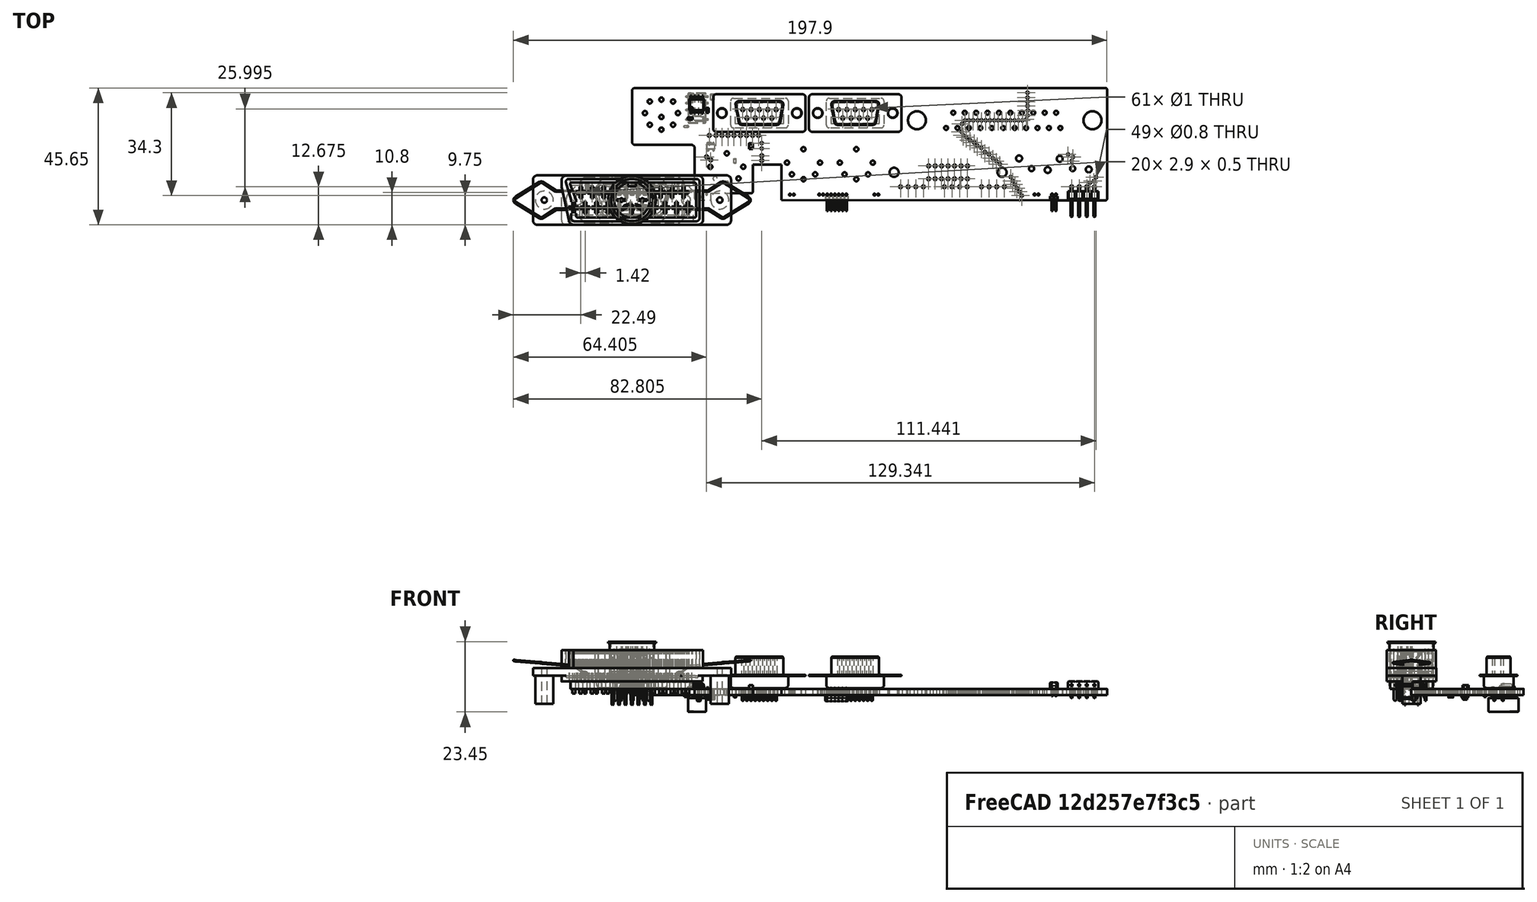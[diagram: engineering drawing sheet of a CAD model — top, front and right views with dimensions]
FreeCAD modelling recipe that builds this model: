
FCSTD DOCUMENT  (FreeCAD 0.20R29177 (Git))
Label: Ultra-IO-shield-2
License: All rights reserved
LicenseURL: http://en.wikipedia.org/wiki/All_rights_reserved
objects: Part::Feature×85, App::Link×60, App::Part×16, PartDesign::CoordinateSystem×1, Sketcher::SketchObject×1
note: 87 computed .brp shape members not serialized (recipe doc carries the construction recipe); baked Part::Feature solids carry a one-line shape summary decoded from their .brp

FEATURE [PartDesign::CoordinateSystem] Local_CS_8e65
  AttacherType = Attacher::AttachEngine3D
FEATURE [Part::Feature] Pcb_8e65
  Placement = pos=(-90.355,111.3,0) rot=(0,0,1;0rad)
  shape: bbox 158.3 x 37.53 x 2 mm, 212 faces (baked)
FEATURE [Sketcher::SketchObject] PCB_Sketch_8e65
  FullyConstrained = false
  sketch-geometry (81):
    g0: LineSegment StartX=40.245 StartY=11.8 StartZ=0 EndX=49.845 EndY=11.8 EndZ=0
    g1: LineSegment StartX=21.345 StartY=8e-16 StartZ=0 EndX=26.245 EndY=0 EndZ=0
    g2: LineSegment StartX=1 StartY=37.4 StartZ=0 EndX=157.845 EndY=37.4 EndZ=0
    g3: LineSegment StartX=49.845 StartY=-0.018571 StartZ=0 EndX=157.845 EndY=-0.13 EndZ=0
    g4: LineSegment StartX=40.245 StartY=11.8 StartZ=0 EndX=40.245 EndY=2.7375 EndZ=0
    g5: LineSegment StartX=20.845 StartY=0.5 StartZ=0 EndX=20.845 EndY=17.4 EndZ=0
    g6: LineSegment StartX=1 StartY=18.4 StartZ=0 EndX=19.845 EndY=18.4 EndZ=0
    g7: LineSegment StartX=1.7e-15 StartY=36.4 StartZ=0 EndX=-8e-16 EndY=19.4 EndZ=0
    g8: LineSegment StartX=26.245 StartY=2.2375 StartZ=0 EndX=39.745 EndY=2.2375 EndZ=0
    g9: LineSegment StartX=26.245 StartY=2.2375 StartZ=0 EndX=26.245 EndY=0 EndZ=0
    g10: LineSegment StartX=158.345 StartY=36.9 StartZ=0 EndX=158.345 EndY=0.37 EndZ=0
    g11: LineSegment StartX=49.845 StartY=11.8 StartZ=0 EndX=49.845 EndY=-0.018571 EndZ=0
    g12: ArcOfCircle CenterX=39.745 CenterY=2.7375 CenterZ=0 NormalX=0 NormalY=0 NormalZ=-1 AngleXU=-3.14159 Radius=0.500001 StartAngle=0 EndAngle=1.57079
    g13: ArcOfCircle CenterX=0.999999 CenterY=36.4 CenterZ=0 NormalX=0 NormalY=0 NormalZ=-1 AngleXU=-7.47076e-07 Radius=0.999999 StartAngle=0 EndAngle=1.5708
    g14: ArcOfCircle CenterX=157.845 CenterY=36.9 CenterZ=0 NormalX=0 NormalY=0 NormalZ=-1 AngleXU=1.5708 Radius=0.500001 StartAngle=0 EndAngle=1.57079
    g15: ArcOfCircle CenterX=21.345 CenterY=0.500001 CenterZ=0 NormalX=0 NormalY=0 NormalZ=-1 AngleXU=-1.57079 Radius=0.500001 StartAngle=0 EndAngle=1.57079
    g16: ArcOfCircle CenterX=0.999999 CenterY=19.4 CenterZ=0 NormalX=0 NormalY=0 NormalZ=-1 AngleXU=-1.5708 Radius=0.999999 StartAngle=0 EndAngle=1.5708
    g17: ArcOfCircle CenterX=19.845 CenterY=17.4 CenterZ=0 NormalX=0 NormalY=0 NormalZ=-1 AngleXU=1.5708 Radius=0.999999 StartAngle=0 EndAngle=1.5708
    g18: ArcOfCircle CenterX=157.845 CenterY=0.370001 CenterZ=0 NormalX=0 NormalY=0 NormalZ=-1 AngleXU=-3.14159 Radius=0.500001 StartAngle=0 EndAngle=1.57079
    g19: Circle CenterX=128.845 CenterY=26.6 CenterZ=0 NormalX=0 NormalY=0 NormalZ=1 AngleXU=0 Radius=0.4
    g20: Circle CenterX=33.9825 CenterY=21.5625 CenterZ=0 NormalX=0 NormalY=0 NormalZ=1 AngleXU=0 Radius=0.5
    g21: Circle CenterX=27.9825 CenterY=21.5625 CenterZ=0 NormalX=0 NormalY=0 NormalZ=1 AngleXU=0 Radius=0.5
    g22: Circle CenterX=131.445 CenterY=26.9 CenterZ=0 NormalX=0 NormalY=0 NormalZ=1 AngleXU=0 Radius=0.4
    g23: Circle CenterX=131.845 CenterY=35.8 CenterZ=0 NormalX=0 NormalY=0 NormalZ=1 AngleXU=0 Radius=0.4
    g24: Circle CenterX=152.686 CenterY=5.82926 CenterZ=0 NormalX=0 NormalY=0 NormalZ=1 AngleXU=0 Radius=0.4
    g25: Circle CenterX=25.7825 CenterY=21.5625 CenterZ=0 NormalX=0 NormalY=0 NormalZ=1 AngleXU=0 Radius=0.5
    g26: Circle CenterX=122.645 CenterY=12 CenterZ=0 NormalX=0 NormalY=0 NormalZ=1 AngleXU=0 Radius=0.4
    g27: Circle CenterX=154.686 CenterY=7.62926 CenterZ=0 NormalX=0 NormalY=0 NormalZ=1 AngleXU=0 Radius=0.4
    g28: Circle CenterX=112.345 CenterY=26.6 CenterZ=0 NormalX=0 NormalY=0 NormalZ=1 AngleXU=0 Radius=0.4
    g29: Circle CenterX=43.245 CenterY=17.2 CenterZ=0 NormalX=0 NormalY=0 NormalZ=1 AngleXU=0 Radius=0.4
    g30: Circle CenterX=42.1825 CenterY=21.5625 CenterZ=0 NormalX=0 NormalY=0 NormalZ=1 AngleXU=0 Radius=0.5
    g31: Circle CenterX=110.045 CenterY=25.4 CenterZ=0 NormalX=0 NormalY=0 NormalZ=1 AngleXU=0 Radius=0.4
    g32: Circle CenterX=129.145 CenterY=2.8 CenterZ=0 NormalX=0 NormalY=0 NormalZ=1 AngleXU=0 Radius=0.4
    g33: Circle CenterX=43.245 CenterY=14.8 CenterZ=0 NormalX=0 NormalY=0 NormalZ=1 AngleXU=0 Radius=0.5
    g34: Circle CenterX=43.245 CenterY=13.2 CenterZ=0 NormalX=0 NormalY=0 NormalZ=1 AngleXU=0 Radius=0.5
    g35: Circle CenterX=109.845 CenterY=22.8 CenterZ=0 NormalX=0 NormalY=0 NormalZ=1 AngleXU=0 Radius=0.4
    g36: Circle CenterX=115.045 CenterY=18.2 CenterZ=0 NormalX=0 NormalY=0 NormalZ=1 AngleXU=0 Radius=0.4
    g37: Circle CenterX=43.245 CenterY=19 CenterZ=0 NormalX=0 NormalY=0 NormalZ=1 AngleXU=0 Radius=0.4
    g38: Circle CenterX=113.745 CenterY=26.6 CenterZ=0 NormalX=0 NormalY=0 NormalZ=1 AngleXU=0 Radius=0.4
    g39: Circle CenterX=145.386 CenterY=15.2293 CenterZ=0 NormalX=0 NormalY=0 NormalZ=1 AngleXU=0 Radius=0.4
    g40: Circle CenterX=117.645 CenterY=16 CenterZ=0 NormalX=0 NormalY=0 NormalZ=1 AngleXU=0 Radius=0.4
    g41: Circle CenterX=110.445 CenterY=21.6 CenterZ=0 NormalX=0 NormalY=0 NormalZ=1 AngleXU=0 Radius=0.4
    g42: Circle CenterX=40.1825 CenterY=21.5625 CenterZ=0 NormalX=0 NormalY=0 NormalZ=1 AngleXU=0 Radius=0.5
    g43: Circle CenterX=120.245 CenterY=14 CenterZ=0 NormalX=0 NormalY=0 NormalZ=1 AngleXU=0 Radius=0.4
    g44: Circle CenterX=122.045 CenterY=26.6 CenterZ=0 NormalX=0 NormalY=0 NormalZ=1 AngleXU=0 Radius=0.4
    g45: Circle CenterX=116.545 CenterY=26.6 CenterZ=0 NormalX=0 NormalY=0 NormalZ=1 AngleXU=0 Radius=0.4
    g46: Circle CenterX=112.645 CenterY=20 CenterZ=0 NormalX=0 NormalY=0 NormalZ=1 AngleXU=0 Radius=0.4
    g47: Circle CenterX=153.986 CenterY=6.32926 CenterZ=0 NormalX=0 NormalY=0 NormalZ=1 AngleXU=0 Radius=0.4
    g48: Circle CenterX=115.245 CenterY=26.6 CenterZ=0 NormalX=0 NormalY=0 NormalZ=1 AngleXU=0 Radius=0.4
    g49: Circle CenterX=126.245 CenterY=7.7 CenterZ=0 NormalX=0 NormalY=0 NormalZ=1 AngleXU=0 Radius=0.4
    g50: Circle CenterX=119.045 CenterY=15.2 CenterZ=0 NormalX=0 NormalY=0 NormalZ=1 AngleXU=0 Radius=0.4
    g51: Circle CenterX=29.9825 CenterY=21.5625 CenterZ=0 NormalX=0 NormalY=0 NormalZ=1 AngleXU=0 Radius=0.5
    g52: Circle CenterX=128.345 CenterY=4 CenterZ=0 NormalX=0 NormalY=0 NormalZ=1 AngleXU=0 Radius=0.4
    g53: Circle CenterX=124.745 CenterY=26.6 CenterZ=0 NormalX=0 NormalY=0 NormalZ=1 AngleXU=0 Radius=0.4
    g54: Circle CenterX=127.645 CenterY=5.2 CenterZ=0 NormalX=0 NormalY=0 NormalZ=1 AngleXU=0 Radius=0.4
    g55: Circle CenterX=126.145 CenterY=26.6 CenterZ=0 NormalX=0 NormalY=0 NormalZ=1 AngleXU=0 Radius=0.4
    g56: Circle CenterX=114.045 CenterY=19.2 CenterZ=0 NormalX=0 NormalY=0 NormalZ=1 AngleXU=0 Radius=0.4
    g57: Circle CenterX=111.045 CenterY=26.6 CenterZ=0 NormalX=0 NormalY=0 NormalZ=1 AngleXU=0 Radius=0.4
    g58: Circle CenterX=131.845 CenterY=32.8 CenterZ=0 NormalX=0 NormalY=0 NormalZ=1 AngleXU=0 Radius=0.4
    g59: Circle CenterX=131.945 CenterY=29.9 CenterZ=0 NormalX=0 NormalY=0 NormalZ=1 AngleXU=0 Radius=0.4
    g60: Circle CenterX=146.586 CenterY=13.0293 CenterZ=0 NormalX=0 NormalY=0 NormalZ=1 AngleXU=0 Radius=0.4
    g61: Circle CenterX=146.986 CenterY=14.3293 CenterZ=0 NormalX=0 NormalY=0 NormalZ=1 AngleXU=0 Radius=0.4
    g62: Circle CenterX=120.745 CenterY=26.6 CenterZ=0 NormalX=0 NormalY=0 NormalZ=1 AngleXU=0 Radius=0.4
    g63: Circle CenterX=131.845 CenterY=34.2 CenterZ=0 NormalX=0 NormalY=0 NormalZ=1 AngleXU=0 Radius=0.4
    g64: Circle CenterX=24.845 CenterY=14.4 CenterZ=0 NormalX=0 NormalY=0 NormalZ=1 AngleXU=0 Radius=0.5
    g65: Circle CenterX=38.1825 CenterY=21.5625 CenterZ=0 NormalX=0 NormalY=0 NormalZ=1 AngleXU=0 Radius=0.5
    g66: Circle CenterX=116.445 CenterY=17.4 CenterZ=0 NormalX=0 NormalY=0 NormalZ=1 AngleXU=0 Radius=0.4
    g67: Circle CenterX=111.445 CenterY=21 CenterZ=0 NormalX=0 NormalY=0 NormalZ=1 AngleXU=0 Radius=0.4
    g68: Circle CenterX=130.145 CenterY=26.6 CenterZ=0 NormalX=0 NormalY=0 NormalZ=1 AngleXU=0 Radius=0.4
    g69: Circle CenterX=129.945 CenterY=1.5 CenterZ=0 NormalX=0 NormalY=0 NormalZ=1 AngleXU=0 Radius=0.4
    g70: Circle CenterX=123.345 CenterY=26.6 CenterZ=0 NormalX=0 NormalY=0 NormalZ=1 AngleXU=0 Radius=0.4
    g71: Circle CenterX=26.245 CenterY=13.4 CenterZ=0 NormalX=0 NormalY=0 NormalZ=1 AngleXU=0 Radius=0.5
    g72: Circle CenterX=131.845 CenterY=31.4 CenterZ=0 NormalX=0 NormalY=0 NormalZ=1 AngleXU=0 Radius=0.4
    g73: Circle CenterX=121.445 CenterY=13 CenterZ=0 NormalX=0 NormalY=0 NormalZ=1 AngleXU=0 Radius=0.4
    g74: Circle CenterX=119.345 CenterY=26.6 CenterZ=0 NormalX=0 NormalY=0 NormalZ=1 AngleXU=0 Radius=0.4
    g75: Circle CenterX=31.9825 CenterY=21.5625 CenterZ=0 NormalX=0 NormalY=0 NormalZ=1 AngleXU=0 Radius=0.5
    g76: Circle CenterX=117.945 CenterY=26.6 CenterZ=0 NormalX=0 NormalY=0 NormalZ=1 AngleXU=0 Radius=0.4
    g77: Circle CenterX=131.845 CenterY=28.2 CenterZ=0 NormalX=0 NormalY=0 NormalZ=1 AngleXU=0 Radius=0.4
    g78: Circle CenterX=126.945 CenterY=6.4 CenterZ=0 NormalX=0 NormalY=0 NormalZ=1 AngleXU=0 Radius=0.4
    g79: Circle CenterX=36.1825 CenterY=21.5625 CenterZ=0 NormalX=0 NormalY=0 NormalZ=1 AngleXU=0 Radius=0.5
    g80: Circle CenterX=127.545 CenterY=26.6 CenterZ=0 NormalX=0 NormalY=0 NormalZ=1 AngleXU=0 Radius=0.4
  constraints (19):
    c: Coincident(g7,g16)
    c: Coincident(g7,g13)
    c: Coincident(g6,g16)
    c: Coincident(g2,g13)
    c: Coincident(g6,g17)
    c: Coincident(g5,g15)
    c: Coincident(g5,g17)
    c: Coincident(g1,g15)
    c: Coincident(g1,g9)
    c: Coincident(g8,g9)
    c: Coincident(g8,g12)
    c: Coincident(g4,g12)
    c: Coincident(g0,g4)
    c: Coincident(g3,g11)
    c: Coincident(g0,g11)
    c: Coincident(g3,g18)
    c: Coincident(g2,g14)
    c: Coincident(g10,g18)
    c: Coincident(g10,g14)
FEATURE [App::Part] Board_Geoms_8e65
  Group = -> [Local_CS_8e65,Pcb_8e65,PCB_Sketch_8e65]
  Origin = -> Origin
FEATURE [Part::Feature] Shape  label="C8_C_0805_2012Metric_f3a3f0892716"
  Placement = pos=(39.645,18,0) rot=(0,0,1;1.5708rad)
  shape: bbox 1.25 x 2 x 1.25 mm, 28 faces (baked)
FEATURE [Part::Feature] Shape001  label="J5_PinHeader_1x02_P127mm_Horizontal_92fba9bb2b89"
  Placement = pos=(141.295,1.825,0) rot=(0,0,-1;1.5708rad)
  shape: bbox 2.54 x 5.7 x 4.5 mm, 58 faces (baked)
FEATURE [Part::Feature] Shape002  label="R18_R_0603_1608Metric_d753575270ea"
  Placement = pos=(25.145,29.9,0) rot=(0,0,-1;1.5708rad)
  shape: bbox 0.8 x 1.6 x 0.45 mm, 26 faces (baked)
FEATURE [App::Link] J5_PinHeader_1x02_P127mm_Horizontal_92fba9bb2b89_ln_  label="J15_PinHeader_1x02_P127mm_Horizontal_528f91ba52fb"
  LinkPlacement = pos=(82.095,1.825,0) rot=(0,0,-1;1.5708rad)
  LinkedObject = -> Shape001
  Placement = pos=(82.095,1.825,0) rot=(0,0,-1;1.5708rad)
FEATURE [App::Link] R18_R_0603_1608Metric_d753575270ea_ln_  label="R14_R_0603_1608Metric_37574bb4476b"
  LinkPlacement = pos=(22.845,25.6,0) rot=(0,0,1;0rad)
  LinkedObject = -> Shape002
  Placement = pos=(22.845,25.6,0) rot=(0,0,1;0rad)
FEATURE [Part::Feature] Part__Feature  label="Plastic-insert"
  Placement = pos=(0,0,0.05) rot=(0,0,1;0rad)
  shape: bbox 22.57 x 11.5 x 12.3 mm, 343 faces (baked)
FEATURE [Part::Feature] Part__Feature001  label="chassis-metal"
  Placement = pos=(0,0,4.5) rot=(0,0,1;0rad)
  shape: bbox 43.9 x 15.3 x 12.3 mm, 159 faces (baked)
FEATURE [Part::Feature] Part__Feature002  label="base-pin"
  Placement = pos=(-6.48,0,4.5) rot=(0,0,1;0rad)
  shape: bbox 1.5 x 1.495 x 17.96 mm, 46 faces (baked)
FEATURE [Part::Feature] Part__Feature003  label="base-pin001"
  Placement = pos=(-4.32,0,4.5) rot=(0,0,1;0rad)
  shape: bbox 1.5 x 1.495 x 17.96 mm, 46 faces (baked)
FEATURE [Part::Feature] Part__Feature004  label="base-pin002"
  Placement = pos=(-2.16,0,4.5) rot=(0,0,1;0rad)
  shape: bbox 1.5 x 1.495 x 17.96 mm, 46 faces (baked)
FEATURE [Part::Feature] Part__Feature005  label="base-pin003"
  Placement = pos=(0,0,4.5) rot=(0,0,1;0rad)
  shape: bbox 1.5 x 1.495 x 17.96 mm, 46 faces (baked)
FEATURE [Part::Feature] Part__Feature006  label="base-pin004"
  Placement = pos=(2.16,0,4.5) rot=(0,0,1;0rad)
  shape: bbox 1.5 x 1.495 x 17.96 mm, 46 faces (baked)
FEATURE [Part::Feature] Part__Feature007  label="base-pin005"
  Placement = pos=(4.32,0,4.5) rot=(0,0,1;0rad)
  shape: bbox 1.5 x 1.495 x 17.96 mm, 46 faces (baked)
FEATURE [Part::Feature] Part__Feature008  label="base-pin006"
  Placement = pos=(6.48,0,4.5) rot=(0,0,1;0rad)
  shape: bbox 1.5 x 1.495 x 17.96 mm, 46 faces (baked)
FEATURE [App::Part] pins_top  label="pins-top"
  Group = -> [Part__Feature002,Part__Feature003,Part__Feature004,Part__Feature005,Part__Feature006,Part__Feature007,Part__Feature008]
  Origin = -> Origin008
FEATURE [Part::Feature] Part__Feature009  label="pins-bot"
  Placement = pos=(0,0,0) rot=(0,0,1;3.14159rad)
  shape: bbox 1.5 x 1.495 x 17.96 mm, 46 faces (baked)
FEATURE [Part::Feature] Part__Feature010  label="pins-bot001"
  Placement = pos=(0,0,0) rot=(0,0,1;3.14159rad)
  shape: bbox 1.5 x 1.495 x 17.96 mm, 46 faces (baked)
FEATURE [Part::Feature] Part__Feature011  label="pins-bot002"
  Placement = pos=(0,0,0) rot=(0,0,1;3.14159rad)
  shape: bbox 1.5 x 1.495 x 17.96 mm, 46 faces (baked)
FEATURE [Part::Feature] Part__Feature012  label="pins-bot003"
  Placement = pos=(0,0,0) rot=(0,0,1;3.14159rad)
  shape: bbox 1.5 x 1.495 x 17.96 mm, 46 faces (baked)
FEATURE [Part::Feature] Part__Feature013  label="pins-bot004"
  Placement = pos=(0,0,0) rot=(0,0,1;3.14159rad)
  shape: bbox 1.5 x 1.495 x 17.96 mm, 46 faces (baked)
FEATURE [Part::Feature] Part__Feature014  label="pins-bot005"
  Placement = pos=(0,0,0) rot=(0,0,1;3.14159rad)
  shape: bbox 1.5 x 1.495 x 17.96 mm, 46 faces (baked)
FEATURE [Part::Feature] Part__Feature015  label="pins-bot006"
  Placement = pos=(0,0,0) rot=(0,0,1;3.14159rad)
  shape: bbox 1.5 x 1.495 x 17.96 mm, 46 faces (baked)
FEATURE [App::Part] pins_bot  label="pins-bot007"
  Group = -> [Part__Feature009,Part__Feature010,Part__Feature011,Part__Feature012,Part__Feature013,Part__Feature014,Part__Feature015]
  Origin = -> Origin009
FEATURE [Part::Feature] Part__Feature016  label="fused-handle-tubes"
  shape: bbox 24.46 x 12.5 x 5.12 mm, 52 faces (baked)
FEATURE [Part::Feature] Part__Feature017  label="Handle Left"
  shape: bbox 24.46 x 12.5 x 5.12 mm, 52 faces (baked)
FEATURE [Part::Feature] Part__Feature018  label="Handle Right"
  Placement = pos=(0,0,0) rot=(0,0,1;3.14159rad)
  shape: bbox 24.46 x 12.5 x 5.12 mm, 52 faces (baked)
FEATURE [App::Part] Handles
  Group = -> [Part__Feature016,Part__Feature017,Part__Feature018]
  Origin = -> Origin010
FEATURE [App::Part] Norcomp_111_014_213L001  label="J9_Norcomp_111_014_213L001_9b66603eb921"
  Group = -> [Part__Feature,Part__Feature001,pins_top,pins_bot,Handles]
  Origin = -> Origin011
  Placement = pos=(105.365,9.25,0) rot=(0,0,1;0rad)
FEATURE [Part::Feature] Shape003  label="J3_PinHeader_1x04_P254mm_Horizontal_ad84bd842bec"
  Placement = pos=(154.186,4.42926,0) rot=(0,0,-1;1.5708rad)
  shape: bbox 10.16 x 10.36 x 5.54 mm, 112 faces (baked)
FEATURE [Part::Feature] Part__Feature019  label="Plastic-body"
  Placement = pos=(0,0,7) rot=(0,0,1;0rad)
  shape: bbox 66 x 16.5 x 17.9 mm, 446 faces (baked)
FEATURE [Part::Feature] Part__Feature020  label="pin-top"
  Placement = pos=(2.38,5.0875,0) rot=(0,0,1;0rad)
  shape: bbox 2.8 x 0.4 x 14.4 mm, 20 faces (baked)
FEATURE [Part::Feature] Part__Feature021  label="pin-top001"
  Placement = pos=(6.18,5.0875,0) rot=(0,0,1;0rad)
  shape: bbox 2.8 x 0.4 x 14.4 mm, 20 faces (baked)
FEATURE [Part::Feature] Part__Feature022  label="pin-top002"
  Placement = pos=(9.98,5.0875,0) rot=(0,0,1;0rad)
  shape: bbox 2.8 x 0.4 x 14.4 mm, 20 faces (baked)
FEATURE [Part::Feature] Part__Feature023  label="pin-top003"
  Placement = pos=(13.78,5.0875,0) rot=(0,0,1;0rad)
  shape: bbox 2.8 x 0.4 x 14.4 mm, 20 faces (baked)
FEATURE [Part::Feature] Part__Feature024  label="pin-top004"
  Placement = pos=(17.58,5.0875,0) rot=(0,0,1;0rad)
  shape: bbox 2.8 x 0.4 x 14.4 mm, 20 faces (baked)
FEATURE [Part::Feature] Part__Feature025  label="pin-top005"
  Placement = pos=(21.38,5.0875,0) rot=(0,0,1;0rad)
  shape: bbox 2.8 x 0.4 x 14.4 mm, 20 faces (baked)
FEATURE [Part::Feature] Part__Feature026  label="pin-top006"
  Placement = pos=(25.18,5.0875,0) rot=(0,0,1;0rad)
  shape: bbox 2.8 x 0.4 x 14.4 mm, 20 faces (baked)
FEATURE [Part::Feature] Part__Feature027  label="pin-top007"
  Placement = pos=(28.98,5.0875,0) rot=(0,0,1;0rad)
  shape: bbox 2.8 x 0.4 x 14.4 mm, 20 faces (baked)
FEATURE [Part::Feature] Part__Feature028  label="pin-top008"
  Placement = pos=(32.78,5.0875,0) rot=(0,0,1;0rad)
  shape: bbox 2.8 x 0.4 x 14.4 mm, 20 faces (baked)
FEATURE [Part::Feature] Part__Feature029  label="pin-top009"
  Placement = pos=(36.58,5.0875,0) rot=(0,0,1;0rad)
  shape: bbox 2.8 x 0.4 x 14.4 mm, 20 faces (baked)
FEATURE [App::Part] top_pins  label="top-pins"
  Group = -> [Part__Feature020,Part__Feature021,Part__Feature022,Part__Feature023,Part__Feature024,Part__Feature025,Part__Feature026,Part__Feature027,Part__Feature028,Part__Feature029]
  Origin = -> Origin012
FEATURE [Part::Feature] Part__Feature030  label="Pin-bot"
  shape: bbox 2.8 x 0.4 x 14.4 mm, 20 faces (baked)
FEATURE [Part::Feature] Part__Feature031  label="Pin-bot001"
  Placement = pos=(3.8,0,0) rot=(0,0,1;0rad)
  shape: bbox 2.8 x 0.4 x 14.4 mm, 20 faces (baked)
FEATURE [Part::Feature] Part__Feature032  label="Pin-bot002"
  Placement = pos=(7.6,0,0) rot=(0,0,1;0rad)
  shape: bbox 2.8 x 0.4 x 14.4 mm, 20 faces (baked)
FEATURE [Part::Feature] Part__Feature033  label="Pin-bot003"
  Placement = pos=(11.4,0,0) rot=(0,0,1;0rad)
  shape: bbox 2.8 x 0.4 x 14.4 mm, 20 faces (baked)
FEATURE [Part::Feature] Part__Feature034  label="Pin-bot004"
  Placement = pos=(15.2,0,0) rot=(0,0,1;0rad)
  shape: bbox 2.8 x 0.4 x 14.4 mm, 20 faces (baked)
FEATURE [Part::Feature] Part__Feature035  label="Pin-bot005"
  Placement = pos=(19,0,0) rot=(0,0,1;0rad)
  shape: bbox 2.8 x 0.4 x 14.4 mm, 20 faces (baked)
FEATURE [Part::Feature] Part__Feature036  label="Pin-bot006"
  Placement = pos=(22.8,0,0) rot=(0,0,1;0rad)
  shape: bbox 2.8 x 0.4 x 14.4 mm, 20 faces (baked)
FEATURE [Part::Feature] Part__Feature037  label="Pin-bot007"
  Placement = pos=(26.6,0,0) rot=(0,0,1;0rad)
  shape: bbox 2.8 x 0.4 x 14.4 mm, 20 faces (baked)
FEATURE [Part::Feature] Part__Feature038  label="Pin-bot008"
  Placement = pos=(30.4,0,0) rot=(0,0,1;0rad)
  shape: bbox 2.8 x 0.4 x 14.4 mm, 20 faces (baked)
FEATURE [Part::Feature] Part__Feature039  label="Pin-bot009"
  Placement = pos=(34.2,0,0) rot=(0,0,1;0rad)
  shape: bbox 2.8 x 0.4 x 14.4 mm, 20 faces (baked)
FEATURE [Part::Feature] Part__Feature040  label="Pin-bot010"
  Placement = pos=(38,0,0) rot=(0,0,1;0rad)
  shape: bbox 2.8 x 0.4 x 14.4 mm, 20 faces (baked)
FEATURE [App::Part] Array001
  Group = -> [Part__Feature030,Part__Feature031,Part__Feature032,Part__Feature033,Part__Feature034,Part__Feature035,Part__Feature036,Part__Feature037,Part__Feature038,Part__Feature039,Part__Feature040]
  Origin = -> Origin013
FEATURE [App::Part] TC_1578891_scart  label="J11_TC_1578891_scart_58c3af9e474b"
  Group = -> [Part__Feature019,top_pins,Array001]
  Origin = -> Origin014
  Placement = pos=(124.245,26.6,0) rot=(0,0,1;0rad)
FEATURE [App::Link] J5_PinHeader_1x02_P127mm_Horizontal_92fba9bb2b89_ln_001  label="J8_PinHeader_1x02_P127mm_Horizontal_95e3cfd9992e"
  LinkPlacement = pos=(24.845,2,0) rot=(0,0,-1;1.5708rad)
  LinkedObject = -> Shape001
  Placement = pos=(24.845,2,0) rot=(0,0,-1;1.5708rad)
FEATURE [App::Link] R18_R_0603_1608Metric_d753575270ea_ln_001  label="R13_R_0603_1608Metric_17f6bcc38b57"
  LinkPlacement = pos=(22.445,27.1,0) rot=(0,0,1;3.14159rad)
  LinkedObject = -> Shape002
  Placement = pos=(22.445,27.1,0) rot=(0,0,1;3.14159rad)
FEATURE [App::Link] R18_R_0603_1608Metric_d753575270ea_ln_002  label="R24_R_0603_1608Metric_963b0f126aa1"
  LinkPlacement = pos=(139.345,15.6,0) rot=(0,0,-1;1.5708rad)
  LinkedObject = -> Shape002
  Placement = pos=(139.345,15.6,0) rot=(0,0,-1;1.5708rad)
FEATURE [Part::Feature] Shape004  label="C9_C_0603_1608Metric_5d00f7ebd9ff"
  Placement = pos=(19.42,27.2,0) rot=(0,0,1;0rad)
  shape: bbox 1.6 x 0.8 x 0.8 mm, 28 faces (baked)
FEATURE [App::Link] R18_R_0603_1608Metric_d753575270ea_ln_003  label="R25_R_0603_1608Metric_11e94d22449a"
  LinkPlacement = pos=(152.545,15.4,0) rot=(0,0,1;2.35619rad)
  LinkedObject = -> Shape002
  Placement = pos=(152.545,15.4,0) rot=(0,0,1;2.35619rad)
FEATURE [Part::Feature] Shape005  label="U1_SOIC_8_39x49mm_P127mm_c3ebf6cbc819"
  Placement = pos=(21.545,31.8,0) rot=(0,0,1;1.5708rad)
  shape: bbox 4.9 x 6 x 1.75 mm, 156 faces (baked)
FEATURE [App::Link] R18_R_0603_1608Metric_d753575270ea_ln_004  label="R17_R_0603_1608Metric_099708a927e8"
  LinkPlacement = pos=(21.145,24.1,0) rot=(0,0,1;0rad)
  LinkedObject = -> Shape002
  Placement = pos=(21.145,24.1,0) rot=(0,0,1;0rad)
FEATURE [App::Link] J5_PinHeader_1x02_P127mm_Horizontal_92fba9bb2b89_ln_002  label="J20_PinHeader_1x02_P127mm_Horizontal_2fb3938f7bfa"
  LinkPlacement = pos=(63.695,1.825,0) rot=(0,0,-1;1.5708rad)
  LinkedObject = -> Shape001
  Placement = pos=(63.695,1.825,0) rot=(0,0,-1;1.5708rad)
FEATURE [App::Link] R18_R_0603_1608Metric_d753575270ea_ln_005  label="R9_R_0603_1608Metric_9ca75bf1930e"
  LinkPlacement = pos=(117.245,31.3,-2) rot=(1,0,0;3.14159rad)
  LinkedObject = -> Shape002
  Placement = pos=(117.245,31.3,-2) rot=(1,0,0;3.14159rad)
FEATURE [App::Link] R18_R_0603_1608Metric_d753575270ea_ln_006  label="R5_R_0603_1608Metric_3b9ff31e242c"
  LinkPlacement = pos=(63.945,7.5,-2) rot=(0.92388,0.382683,0;3.14159rad)
  LinkedObject = -> Shape002
  Placement = pos=(63.945,7.5,-2) rot=(0.92388,0.382683,0;3.14159rad)
FEATURE [App::Link] C9_C_0603_1608Metric_5d00f7ebd9ff_ln_  label="C1_C_0603_1608Metric_6e1e9fd61820"
  LinkPlacement = pos=(72.995,19.55,-2) rot=(0.92388,0.382683,0;3.14159rad)
  LinkedObject = -> Shape004
  Placement = pos=(72.995,19.55,-2) rot=(0.92388,0.382683,0;3.14159rad)
FEATURE [App::Link] R18_R_0603_1608Metric_d753575270ea_ln_007  label="R11_R_0603_1608Metric_f6652046c7d5"
  LinkPlacement = pos=(16.445,35.2,-2) rot=(0.707107,-0.707107,0;3.14159rad)
  LinkedObject = -> Shape002
  Placement = pos=(16.445,35.2,-2) rot=(0.707107,-0.707107,0;3.14159rad)
FEATURE [Part::Feature] Shape006  label="R12_R_0805_2012Metric_fea975d0d3e0"
  Placement = pos=(26.845,34.4,-2) rot=(0.707107,0.707107,0;3.14159rad)
  shape: bbox 1.2 x 2 x 0.45 mm, 26 faces (baked)
FEATURE [Part::Feature] Shape007  label="FB2_L_0603_1608Metric_618cee020b58"
  Placement = pos=(34.345,13.1,-2) rot=(0.707107,0.707107,0;3.14159rad)
  shape: bbox 0.8 x 1.6 x 0.8 mm, 28 faces (baked)
FEATURE [App::Link] J3_PinHeader_1x04_P254mm_Horizontal_ad84bd842bec_ln_  label="J1_PinHeader_1x04_P254mm_Horizontal_e9d8d5db6f15"
  LinkPlacement = pos=(116.515,4.425,-2) rot=(0.707107,-0.707107,0;3.14159rad)
  LinkedObject = -> Shape003
  Placement = pos=(116.515,4.425,-2) rot=(0.707107,-0.707107,0;3.14159rad)
FEATURE [App::Link] C8_C_0805_2012Metric_f3a3f0892716_ln_  label="C4_C_0805_2012Metric_ebac419a7334"
  LinkPlacement = pos=(28.645,13.6,-2) rot=(0,1,0;3.14159rad)
  LinkedObject = -> Shape
  Placement = pos=(28.645,13.6,-2) rot=(0,1,0;3.14159rad)
FEATURE [App::Link] R18_R_0603_1608Metric_d753575270ea_ln_008  label="R28_R_0603_1608Metric_6b7fdb3c0648"
  LinkPlacement = pos=(41.445,33.4,-2) rot=(0.707107,0.707107,0;3.14159rad)
  LinkedObject = -> Shape002
  Placement = pos=(41.445,33.4,-2) rot=(0.707107,0.707107,0;3.14159rad)
FEATURE [App::Link] R18_R_0603_1608Metric_d753575270ea_ln_009  label="R10_R_0603_1608Metric_f5e09943f181"
  LinkPlacement = pos=(86.945,4.1,-2) rot=(0.707107,-0.707107,0;3.14159rad)
  LinkedObject = -> Shape002
  Placement = pos=(86.945,4.1,-2) rot=(0.707107,-0.707107,0;3.14159rad)
FEATURE [App::Link] C9_C_0603_1608Metric_5d00f7ebd9ff_ln_001  label="C3_C_0603_1608Metric_1001c02b6788"
  LinkPlacement = pos=(61.195,19.3,-2) rot=(1,0,0;3.14159rad)
  LinkedObject = -> Shape004
  Placement = pos=(61.195,19.3,-2) rot=(1,0,0;3.14159rad)
FEATURE [App::Link] R18_R_0603_1608Metric_d753575270ea_ln_010  label="R34_R_0603_1608Metric_d53ed4e581f7"
  LinkPlacement = pos=(44.245,25,-2) rot=(0.707107,-0.707107,0;3.14159rad)
  LinkedObject = -> Shape002
  Placement = pos=(44.245,25,-2) rot=(0.707107,-0.707107,0;3.14159rad)
FEATURE [App::Link] R18_R_0603_1608Metric_d753575270ea_ln_011  label="R29_R_0603_1608Metric_2b82e889ab4b"
  LinkPlacement = pos=(39.645,33.4,-2) rot=(0.707107,0.707107,0;3.14159rad)
  LinkedObject = -> Shape002
  Placement = pos=(39.645,33.4,-2) rot=(0.707107,0.707107,0;3.14159rad)
FEATURE [App::Link] C9_C_0603_1608Metric_5d00f7ebd9ff_ln_002  label="C10_C_0603_1608Metric_ea9d92ba4a46"
  LinkPlacement = pos=(12.145,30.8,-2) rot=(0.92388,-0.382683,0;3.14159rad)
  LinkedObject = -> Shape004
  Placement = pos=(12.145,30.8,-2) rot=(0.92388,-0.382683,0;3.14159rad)
FEATURE [App::Link] C8_C_0805_2012Metric_f3a3f0892716_ln_001  label="C2_C_0805_2012Metric_ab2f62712393"
  LinkPlacement = pos=(27.445,24.2,-2) rot=(0.92388,0.382683,0;3.14159rad)
  LinkedObject = -> Shape
  Placement = pos=(27.445,24.2,-2) rot=(0.92388,0.382683,0;3.14159rad)
FEATURE [App::Link] R18_R_0603_1608Metric_d753575270ea_ln_012  label="R30_R_0603_1608Metric_17e547bb5400"
  LinkPlacement = pos=(78.845,33,-2) rot=(0.707107,0.707107,0;3.14159rad)
  LinkedObject = -> Shape002
  Placement = pos=(78.845,33,-2) rot=(0.707107,0.707107,0;3.14159rad)
FEATURE [App::Link] R18_R_0603_1608Metric_d753575270ea_ln_013  label="R15_R_0603_1608Metric_f111bec7f2ee"
  LinkPlacement = pos=(25.545,24.75,-2) rot=(0.92388,0.382683,0;3.14159rad)
  LinkedObject = -> Shape002
  Placement = pos=(25.545,24.75,-2) rot=(0.92388,0.382683,0;3.14159rad)
FEATURE [App::Link] R18_R_0603_1608Metric_d753575270ea_ln_014  label="R7_R_0603_1608Metric_b1d9ba80437c"
  LinkPlacement = pos=(55.045,4.2,-2) rot=(0,1,0;3.14159rad)
  LinkedObject = -> Shape002
  Placement = pos=(55.045,4.2,-2) rot=(0,1,0;3.14159rad)
FEATURE [App::Link] FB2_L_0603_1608Metric_618cee020b58_ln_  label="FB5_L_0603_1608Metric_5cebe498e360"
  LinkPlacement = pos=(52.945,5.75,-2) rot=(0,1,0;3.14159rad)
  LinkedObject = -> Shape007
  Placement = pos=(52.945,5.75,-2) rot=(0,1,0;3.14159rad)
FEATURE [App::Link] R18_R_0603_1608Metric_d753575270ea_ln_015  label="R16_R_0603_1608Metric_98c7d70c461d"
  LinkPlacement = pos=(29.295,23.6,-2) rot=(0.92388,0.382683,0;3.14159rad)
  LinkedObject = -> Shape002
  Placement = pos=(29.295,23.6,-2) rot=(0.92388,0.382683,0;3.14159rad)
FEATURE [App::Link] FB2_L_0603_1608Metric_618cee020b58_ln_001  label="FB4_L_0603_1608Metric_820e8441e16c"
  LinkPlacement = pos=(80.995,8.5,-2) rot=(0.707107,-0.707107,0;3.14159rad)
  LinkedObject = -> Shape007
  Placement = pos=(80.995,8.5,-2) rot=(0.707107,-0.707107,0;3.14159rad)
FEATURE [App::Link] C9_C_0603_1608Metric_5d00f7ebd9ff_ln_003  label="C11_C_0603_1608Metric_40b82c1e5be3"
  LinkPlacement = pos=(6.22,22.2,-2) rot=(1,0,0;3.14159rad)
  LinkedObject = -> Shape004
  Placement = pos=(6.22,22.2,-2) rot=(1,0,0;3.14159rad)
FEATURE [App::Link] C9_C_0603_1608Metric_5d00f7ebd9ff_ln_004  label="C5_C_0603_1608Metric_08e25d952e01"
  LinkPlacement = pos=(26.045,20.4,-2) rot=(1,0,0;3.14159rad)
  LinkedObject = -> Shape004
  Placement = pos=(26.045,20.4,-2) rot=(1,0,0;3.14159rad)
FEATURE [App::Link] FB2_L_0603_1608Metric_618cee020b58_ln_002  label="FB1_L_0603_1608Metric_5dbf3c8ba924"
  LinkPlacement = pos=(63.945,9.75,-2) rot=(0.92388,0.382683,0;3.14159rad)
  LinkedObject = -> Shape007
  Placement = pos=(63.945,9.75,-2) rot=(0.92388,0.382683,0;3.14159rad)
FEATURE [App::Link] R18_R_0603_1608Metric_d753575270ea_ln_016  label="R19_R_0603_1608Metric_90fc13b796ea"
  LinkPlacement = pos=(7.345,29.8,-2) rot=(1,0,0;3.14159rad)
  LinkedObject = -> Shape002
  Placement = pos=(7.345,29.8,-2) rot=(1,0,0;3.14159rad)
FEATURE [App::Link] R18_R_0603_1608Metric_d753575270ea_ln_017  label="R100_R_0603_1608Metric_c06db4a17feb"
  LinkPlacement = pos=(84.8114,14.3664,-2) rot=(-0.382683,0.92388,0;3.14159rad)
  LinkedObject = -> Shape002
  Placement = pos=(84.8114,14.3664,-2) rot=(-0.382683,0.92388,0;3.14159rad)
FEATURE [App::Link] FB2_L_0603_1608Metric_618cee020b58_ln_003  label="FB3_L_0603_1608Metric_6a309daece9a"
  LinkPlacement = pos=(35.695,4.5,-2) rot=(0,1,0;3.14159rad)
  LinkedObject = -> Shape007
  Placement = pos=(35.695,4.5,-2) rot=(0,1,0;3.14159rad)
FEATURE [App::Link] J5_PinHeader_1x02_P127mm_Horizontal_92fba9bb2b89_ln_003  label="J22_PinHeader_1x02_P127mm_Horizontal_3d0318de4f62"
  LinkPlacement = pos=(134.195,1.825,-2) rot=(0.707107,-0.707107,0;3.14159rad)
  LinkedObject = -> Shape001
  Placement = pos=(134.195,1.825,-2) rot=(0.707107,-0.707107,0;3.14159rad)
FEATURE [App::Link] R18_R_0603_1608Metric_d753575270ea_ln_018  label="R8_R_0603_1608Metric_e465b4112c3c"
  LinkPlacement = pos=(113.945,31.3,-2) rot=(1,0,0;3.14159rad)
  LinkedObject = -> Shape002
  Placement = pos=(113.945,31.3,-2) rot=(1,0,0;3.14159rad)
FEATURE [App::Link] R18_R_0603_1608Metric_d753575270ea_ln_019  label="R22_R_0603_1608Metric_9c6b6379f6f2"
  LinkPlacement = pos=(3.645,21.4,-2) rot=(0.707107,0.707107,0;3.14159rad)
  LinkedObject = -> Shape002
  Placement = pos=(3.645,21.4,-2) rot=(0.707107,0.707107,0;3.14159rad)
FEATURE [App::Link] J3_PinHeader_1x04_P254mm_Horizontal_ad84bd842bec_ln_001  label="J18_PinHeader_1x04_P254mm_Horizontal_ed5a7f63db65"
  LinkPlacement = pos=(104.115,4.425,-2) rot=(0.707107,-0.707107,0;3.14159rad)
  LinkedObject = -> Shape003
  Placement = pos=(104.115,4.425,-2) rot=(0.707107,-0.707107,0;3.14159rad)
FEATURE [App::Link] R18_R_0603_1608Metric_d753575270ea_ln_020  label="R2_R_0603_1608Metric_0536453e6189"
  LinkPlacement = pos=(76.245,19.7,-2) rot=(0.92388,-0.382683,0;3.14159rad)
  LinkedObject = -> Shape002
  Placement = pos=(76.245,19.7,-2) rot=(0.92388,-0.382683,0;3.14159rad)
FEATURE [App::Link] R18_R_0603_1608Metric_d753575270ea_ln_021  label="R33_R_0603_1608Metric_89e54b5b2bb2"
  LinkPlacement = pos=(71.645,33,-2) rot=(0.707107,0.707107,0;3.14159rad)
  LinkedObject = -> Shape002
  Placement = pos=(71.645,33,-2) rot=(0.707107,0.707107,0;3.14159rad)
FEATURE [Part::Feature] Shape008  label="J4_PinHeader_1x06_P127mm_Horizontal_35cb890b82b2"
  Placement = pos=(65.07,1.825,-2) rot=(0.707107,-0.707107,0;3.14159rad)
  shape: bbox 7.62 x 5.7 x 4.5 mm, 166 faces (baked)
FEATURE [Part::Feature] Shape009  label="D1_D_SOD_523_85ed3e96afe0"
  Placement = pos=(18.045,24.5,-2) rot=(0,1,0;3.14159rad)
  shape: bbox 1.6 x 0.8 x 0.63 mm, 27 faces (baked)
FEATURE [App::Link] R18_R_0603_1608Metric_d753575270ea_ln_022  label="R36_R_0603_1608Metric_d5d399493403"
  LinkPlacement = pos=(77.545,24.9,-2) rot=(0.707107,-0.707107,0;3.14159rad)
  LinkedObject = -> Shape002
  Placement = pos=(77.545,24.9,-2) rot=(0.707107,-0.707107,0;3.14159rad)
FEATURE [App::Link] R18_R_0603_1608Metric_d753575270ea_ln_023  label="R21_R_0603_1608Metric_c9845f8941b4"
  LinkPlacement = pos=(1.845,23.4,-2) rot=(0.707107,0.707107,0;3.14159rad)
  LinkedObject = -> Shape002
  Placement = pos=(1.845,23.4,-2) rot=(0.707107,0.707107,0;3.14159rad)
FEATURE [App::Link] R18_R_0603_1608Metric_d753575270ea_ln_024  label="R32_R_0603_1608Metric_012f3d9432d4"
  LinkPlacement = pos=(73.445,33,-2) rot=(0.707107,0.707107,0;3.14159rad)
  LinkedObject = -> Shape002
  Placement = pos=(73.445,33,-2) rot=(0.707107,0.707107,0;3.14159rad)
FEATURE [Part::Feature] Shape010  label="J12_PinHeader_1x01_P127mm_Horizontal_8008a05a0a64"
  Placement = pos=(22.245,2.025,-2) rot=(0.707107,-0.707107,0;3.14159rad)
  shape: bbox 1.27 x 5.7 x 4.5 mm, 31 faces (baked)
FEATURE [App::Link] R18_R_0603_1608Metric_d753575270ea_ln_025  label="R31_R_0603_1608Metric_2f390833acca"
  LinkPlacement = pos=(77.045,33,-2) rot=(0.707107,0.707107,0;3.14159rad)
  LinkedObject = -> Shape002
  Placement = pos=(77.045,33,-2) rot=(0.707107,0.707107,0;3.14159rad)
FEATURE [App::Link] J3_PinHeader_1x04_P254mm_Horizontal_ad84bd842bec_ln_002  label="J19_PinHeader_1x04_P254mm_Horizontal_8c37e57248cd"
  LinkPlacement = pos=(89.515,4.425,-2) rot=(0.707107,-0.707107,0;3.14159rad)
  LinkedObject = -> Shape003
  Placement = pos=(89.515,4.425,-2) rot=(0.707107,-0.707107,0;3.14159rad)
FEATURE [App::Link] R18_R_0603_1608Metric_d753575270ea_ln_026  label="R26_R_0603_1608Metric_6aa27b6d2475"
  LinkPlacement = pos=(47.445,33.4,-2) rot=(0.707107,0.707107,0;3.14159rad)
  LinkedObject = -> Shape002
  Placement = pos=(47.445,33.4,-2) rot=(0.707107,0.707107,0;3.14159rad)
FEATURE [App::Link] C9_C_0603_1608Metric_5d00f7ebd9ff_ln_005  label="C7_C_0603_1608Metric_431332e7b39f"
  LinkPlacement = pos=(28.495,10.9,-2) rot=(0.707107,0.707107,0;3.14159rad)
  LinkedObject = -> Shape004
  Placement = pos=(28.495,10.9,-2) rot=(0.707107,0.707107,0;3.14159rad)
FEATURE [App::Link] R18_R_0603_1608Metric_d753575270ea_ln_027  label="R4_R_0603_1608Metric_b2f64a43288f"
  LinkPlacement = pos=(30.095,11.1,-2) rot=(0.707107,0.707107,0;3.14159rad)
  LinkedObject = -> Shape002
  Placement = pos=(30.095,11.1,-2) rot=(0.707107,0.707107,0;3.14159rad)
FEATURE [App::Link] R18_R_0603_1608Metric_d753575270ea_ln_028  label="R1_R_0603_1608Metric_fdd1dcc8b35c"
  LinkPlacement = pos=(83.0616,4.18336,-2) rot=(0.382683,0.92388,0;3.14159rad)
  LinkedObject = -> Shape002
  Placement = pos=(83.0616,4.18336,-2) rot=(0.382683,0.92388,0;3.14159rad)
FEATURE [App::Link] R18_R_0603_1608Metric_d753575270ea_ln_029  label="R23_R_0603_1608Metric_6cce8b24cf85"
  LinkPlacement = pos=(17.745,21.2,-2) rot=(0,1,0;3.14159rad)
  LinkedObject = -> Shape002
  Placement = pos=(17.745,21.2,-2) rot=(0,1,0;3.14159rad)
FEATURE [App::Link] R18_R_0603_1608Metric_d753575270ea_ln_030  label="R35_R_0603_1608Metric_01bacf0335dd"
  LinkPlacement = pos=(46.045,25,-2) rot=(0.707107,-0.707107,0;3.14159rad)
  LinkedObject = -> Shape002
  Placement = pos=(46.045,25,-2) rot=(0.707107,-0.707107,0;3.14159rad)
FEATURE [App::Link] C8_C_0805_2012Metric_f3a3f0892716_ln_002  label="C6_C_0805_2012Metric_d7e7f57bd83f"
  LinkPlacement = pos=(21.945,19.1375,-2) rot=(0.707107,-0.707107,0;3.14159rad)
  LinkedObject = -> Shape
  Placement = pos=(21.945,19.1375,-2) rot=(0.707107,-0.707107,0;3.14159rad)
FEATURE [Part::Feature] Shape011  label="RY1_C-1462037-2_2b60f7be023a"
  Placement = pos=(21.645,30.7,-2) rot=(0,0,1;1.5708rad)
  shape: bbox 7.516 x 10 x 5.65 mm, 115 faces (baked)
FEATURE [Part::Feature] Shape012  label="U2_SOT_23_5_e1dfd6190d34"
  Placement = pos=(26.195,17.8,-2) rot=(0.707107,-0.707107,0;3.14159rad)
  shape: bbox 2.9 x 2.8 x 1.55 mm, 109 faces (baked)
FEATURE [App::Link] C8_C_0805_2012Metric_f3a3f0892716_ln_003  label="C100_C_0805_2012Metric_50f9677266a3"
  LinkPlacement = pos=(86.045,13.1,-2) rot=(0.92388,0.382683,0;3.14159rad)
  LinkedObject = -> Shape
  Placement = pos=(86.045,13.1,-2) rot=(0.92388,0.382683,0;3.14159rad)
FEATURE [App::Link] R18_R_0603_1608Metric_d753575270ea_ln_031  label="R37_R_0603_1608Metric_ae419829358b"
  LinkPlacement = pos=(75.745,24.9,-2) rot=(0.707107,-0.707107,0;3.14159rad)
  LinkedObject = -> Shape002
  Placement = pos=(75.745,24.9,-2) rot=(0.707107,-0.707107,0;3.14159rad)
FEATURE [App::Link] R18_R_0603_1608Metric_d753575270ea_ln_032  label="R3_R_0603_1608Metric_f07b72fade90"
  LinkPlacement = pos=(35.645,16.25,-2) rot=(0,1,0;3.14159rad)
  LinkedObject = -> Shape002
  Placement = pos=(35.645,16.25,-2) rot=(0,1,0;3.14159rad)
FEATURE [App::Link] C9_C_0603_1608Metric_5d00f7ebd9ff_ln_006  label="C12_C_0603_1608Metric_7eee22933b69"
  LinkPlacement = pos=(66.045,28.2,-2) rot=(1,0,0;3.14159rad)
  LinkedObject = -> Shape004
  Placement = pos=(66.045,28.2,-2) rot=(1,0,0;3.14159rad)
FEATURE [App::Link] J5_PinHeader_1x02_P127mm_Horizontal_92fba9bb2b89_ln_004  label="J13_PinHeader_1x02_P127mm_Horizontal_db208a9ea7d4"
  LinkPlacement = pos=(52.645,1.8,-2) rot=(0.707107,-0.707107,0;3.14159rad)
  LinkedObject = -> Shape001
  Placement = pos=(52.645,1.8,-2) rot=(0.707107,-0.707107,0;3.14159rad)
FEATURE [App::Link] R18_R_0603_1608Metric_d753575270ea_ln_033  label="R6_R_0603_1608Metric_d48f2cee73d1"
  LinkPlacement = pos=(61.195,17.8,-2) rot=(0,1,0;3.14159rad)
  LinkedObject = -> Shape002
  Placement = pos=(61.195,17.8,-2) rot=(0,1,0;3.14159rad)
FEATURE [App::Link] R18_R_0603_1608Metric_d753575270ea_ln_034  label="R38_R_0603_1608Metric_c0e5f836ba56"
  LinkPlacement = pos=(66.045,26.6,-2) rot=(0,1,0;3.14159rad)
  LinkedObject = -> Shape002
  Placement = pos=(66.045,26.6,-2) rot=(0,1,0;3.14159rad)
FEATURE [App::Link] R18_R_0603_1608Metric_d753575270ea_ln_035  label="R20_R_0603_1608Metric_71b8a8eb15b5"
  LinkPlacement = pos=(3.445,25.4,-2) rot=(0.707107,0.707107,0;3.14159rad)
  LinkedObject = -> Shape002
  Placement = pos=(3.445,25.4,-2) rot=(0.707107,0.707107,0;3.14159rad)
FEATURE [App::Link] R18_R_0603_1608Metric_d753575270ea_ln_036  label="R27_R_0603_1608Metric_bd650663cc47"
  LinkPlacement = pos=(45.745,33.4,-2) rot=(0.707107,0.707107,0;3.14159rad)
  LinkedObject = -> Shape002
  Placement = pos=(45.745,33.4,-2) rot=(0.707107,0.707107,0;3.14159rad)
FEATURE [App::Part] Bot_8e65
  Group = -> [R18_R_0603_1608Metric_d753575270ea_ln_005,R18_R_0603_1608Metric_d753575270ea_ln_006,C9_C_0603_1608Metric_5d00f7ebd9ff_ln_,R18_R_0603_1608Metric_d753575270ea_ln_007,Shape006,Shape007,J3_PinHeader_1x04_P254mm_Horizontal_ad84bd842bec_ln_,C8_C_0805_2012Metric_f3a3f0892716_ln_,R18_R_0603_1608Metric_d753575270ea_ln_008,R18_R_0603_1608Metric_d753575270ea_ln_009,C9_C_0603_1608Metric_5d00f7ebd9ff_ln_001,+48 more]
  Origin = -> Origin004
FEATURE [Part::Feature] Part__Feature041  label="Casing"
  shape: bbox 18.09 x 18.09 x 19.8 mm, 30 faces (baked)
FEATURE [Part::Feature] Part__Feature042  label="Plastic"
  Placement = pos=(0,0,0) rot=(0,0,1;1.5708rad)
  shape: bbox 13.5 x 13.5 x 13.8 mm, 83 faces (baked)
FEATURE [Part::Feature] Part__Feature043  label="Pin-contact1"
  Placement = pos=(0,0,-4) rot=(0,0,1;0rad)
  shape: bbox 3.9 x 0.55 x 15 mm, 20 faces (baked)
FEATURE [Part::Feature] Part__Feature044  label="Pin-contact002"
  Placement = pos=(0,0,-4) rot=(0,0,1;1.5708rad)
  shape: bbox 0.55 x 3.9 x 15 mm, 20 faces (baked)
FEATURE [Part::Feature] Part__Feature045  label="Pin-contact003"
  Placement = pos=(0,0,-4) rot=(0,0,1;3.14159rad)
  shape: bbox 3.9 x 0.55 x 15 mm, 20 faces (baked)
FEATURE [Part::Feature] Part__Feature046  label="Pin-contact004"
  Placement = pos=(0,0,-4) rot=(0,0,1;0.785398rad)
  shape: bbox 3.147 x 3.147 x 15 mm, 20 faces (baked)
FEATURE [Part::Feature] Part__Feature047  label="Pin-contact005"
  Placement = pos=(0,0,-4) rot=(0,0,1;2.35619rad)
  shape: bbox 3.147 x 3.147 x 15 mm, 20 faces (baked)
FEATURE [App::Part] CUI_SD_50BV
  Group = -> [Part__Feature041,Part__Feature042,Part__Feature043,Part__Feature044,Part__Feature045,Part__Feature046,Part__Feature047]
  Origin = -> Origin015
  Placement = pos=(9.825,28.9,0) rot=(0,0,1;0rad)
FEATURE [Part::Feature] Part__Feature048  label="Casing001"
  shape: bbox 18.09 x 18.09 x 19.8 mm, 30 faces (baked)
FEATURE [Part::Feature] Part__Feature049  label="Plastic001"
  Placement = pos=(0,0,0) rot=(0,0,1;1.5708rad)
  shape: bbox 13.5 x 13.5 x 13.8 mm, 83 faces (baked)
FEATURE [Part::Feature] Part__Feature050  label="Pin-contact006"
  Placement = pos=(0,0,-4) rot=(0,0,1;0rad)
  shape: bbox 3.9 x 0.55 x 15 mm, 20 faces (baked)
FEATURE [Part::Feature] Part__Feature051  label="Pin-contact007"
  Placement = pos=(0,0,-4) rot=(0,0,1;1.5708rad)
  shape: bbox 0.55 x 3.9 x 15 mm, 20 faces (baked)
FEATURE [Part::Feature] Part__Feature052  label="Pin-contact008"
  Placement = pos=(0,0,-4) rot=(0,0,1;3.14159rad)
  shape: bbox 3.9 x 0.55 x 15 mm, 20 faces (baked)
FEATURE [Part::Feature] Part__Feature053  label="Pin-contact009"
  Placement = pos=(0,0,-4) rot=(0,0,1;0.785398rad)
  shape: bbox 3.147 x 3.147 x 15 mm, 20 faces (baked)
FEATURE [Part::Feature] Part__Feature054  label="Pin-contact010"
  Placement = pos=(0,0,-4) rot=(0,0,1;2.35619rad)
  shape: bbox 3.147 x 3.147 x 15 mm, 20 faces (baked)
FEATURE [App::Part] CUI_SD_50BV001
  Group = -> [Part__Feature048,Part__Feature049,Part__Feature050,Part__Feature051,Part__Feature052,Part__Feature053,Part__Feature054]
  Origin = -> Origin016
  Placement = pos=(31.6,11,0) rot=(0,0,1;0rad)
FEATURE [Part::Feature] Part__Feature055  label="Casing002"
  shape: bbox 18.09 x 18.09 x 19.8 mm, 30 faces (baked)
FEATURE [Part::Feature] Part__Feature056  label="Plastic002"
  Placement = pos=(0,0,0) rot=(0,0,1;1.5708rad)
  shape: bbox 13.5 x 13.5 x 13.8 mm, 83 faces (baked)
FEATURE [Part::Feature] Part__Feature057  label="Pin-contact011"
  Placement = pos=(0,0,-4) rot=(0,0,1;0rad)
  shape: bbox 3.9 x 0.55 x 15 mm, 20 faces (baked)
FEATURE [Part::Feature] Part__Feature058  label="Pin-contact012"
  Placement = pos=(0,0,-4) rot=(0,0,1;1.5708rad)
  shape: bbox 0.55 x 3.9 x 15 mm, 20 faces (baked)
FEATURE [Part::Feature] Part__Feature059  label="Pin-contact013"
  Placement = pos=(0,0,-4) rot=(0,0,1;3.14159rad)
  shape: bbox 3.9 x 0.55 x 15 mm, 20 faces (baked)
FEATURE [Part::Feature] Part__Feature060  label="Pin-contact014"
  Placement = pos=(0,0,-4) rot=(0,0,1;0.785398rad)
  shape: bbox 3.147 x 3.147 x 15 mm, 20 faces (baked)
FEATURE [Part::Feature] Part__Feature061  label="Pin-contact015"
  Placement = pos=(0,0,-4) rot=(0,0,1;2.35619rad)
  shape: bbox 3.147 x 3.147 x 15 mm, 20 faces (baked)
FEATURE [App::Part] CUI_SD_50BV002
  Group = -> [Part__Feature055,Part__Feature056,Part__Feature057,Part__Feature058,Part__Feature059,Part__Feature060,Part__Feature061]
  Origin = -> Origin017
  Placement = pos=(57.15,12.4,0) rot=(0,0,1;0rad)
FEATURE [Part::Feature] Part__Feature062  label="Casing003"
  shape: bbox 18.09 x 18.09 x 19.8 mm, 30 faces (baked)
FEATURE [Part::Feature] Part__Feature063  label="Plastic003"
  Placement = pos=(0,0,0) rot=(0,0,1;1.5708rad)
  shape: bbox 13.5 x 13.5 x 13.8 mm, 83 faces (baked)
FEATURE [Part::Feature] Part__Feature064  label="Pin-contact016"
  Placement = pos=(0,0,-4) rot=(0,0,1;0rad)
  shape: bbox 3.9 x 0.55 x 15 mm, 20 faces (baked)
FEATURE [Part::Feature] Part__Feature065  label="Pin-contact017"
  Placement = pos=(0,0,-4) rot=(0,0,1;1.5708rad)
  shape: bbox 0.55 x 3.9 x 15 mm, 20 faces (baked)
FEATURE [Part::Feature] Part__Feature066  label="Pin-contact018"
  Placement = pos=(0,0,-4) rot=(0,0,1;3.14159rad)
  shape: bbox 3.9 x 0.55 x 15 mm, 20 faces (baked)
FEATURE [Part::Feature] Part__Feature067  label="Pin-contact019"
  Placement = pos=(0,0,-4) rot=(0,0,1;0.785398rad)
  shape: bbox 3.147 x 3.147 x 15 mm, 20 faces (baked)
FEATURE [Part::Feature] Part__Feature068  label="Pin-contact020"
  Placement = pos=(0,0,-4) rot=(0,0,1;2.35619rad)
  shape: bbox 3.147 x 3.147 x 15 mm, 20 faces (baked)
FEATURE [App::Part] CUI_SD_50BV003
  Group = -> [Part__Feature062,Part__Feature063,Part__Feature064,Part__Feature065,Part__Feature066,Part__Feature067,Part__Feature068]
  Origin = -> Origin018
  Placement = pos=(74.75,12.4,0) rot=(0,0,1;0rad)
FEATURE [Part::Feature] Part__Feature069  label="DSUB-9_Female_Vertical_P2.77x2.84mm"
  Placement = pos=(79.95,30.45,0) rot=(0,0,1;0rad)
  shape: bbox 30.96 x 12.66 x 14.7 mm, 151 faces (baked)
FEATURE [Part::Feature] Part__Feature070  label="DSUB-9_Female_Vertical_P2.77x2.84mm001"
  Placement = pos=(48,30.45,0) rot=(0,0,1;0rad)
  shape: bbox 30.96 x 12.66 x 14.7 mm, 151 faces (baked)
FEATURE [App::Part] Top_8e65
  Group = -> [Shape,Shape001,Shape002,J5_PinHeader_1x02_P127mm_Horizontal_92fba9bb2b89_ln_,R18_R_0603_1608Metric_d753575270ea_ln_,Norcomp_111_014_213L001,Shape003,TC_1578891_scart,J5_PinHeader_1x02_P127mm_Horizontal_92fba9bb2b89_ln_001,R18_R_0603_1608Metric_d753575270ea_ln_001,R18_R_0603_1608Metric_d753575270ea_ln_002,Shape004,R18_R_0603_1608Metric_d753575270ea_ln_003,Shape005,+8 more]
  Origin = -> Origin003
FEATURE [App::Part] Step_Models_8e65
  Group = -> [Top_8e65,Bot_8e65]
  Origin = -> Origin002
FEATURE [App::Part] Board_8e65  label="Ultra-IO-shield"
  Group = -> [Board_Geoms_8e65,Step_Models_8e65]
  Origin = -> Origin001
